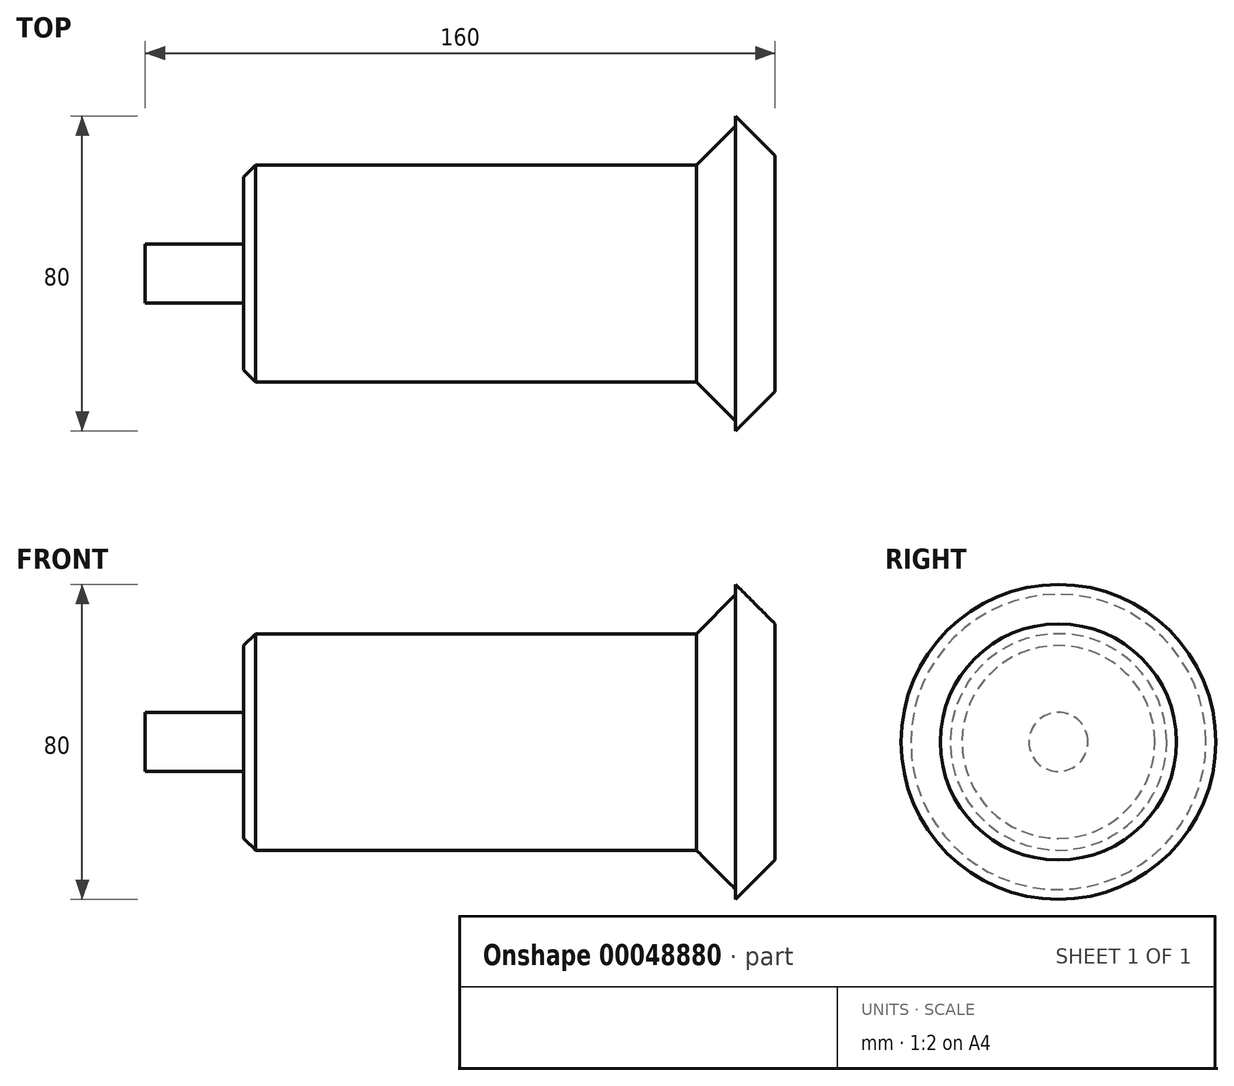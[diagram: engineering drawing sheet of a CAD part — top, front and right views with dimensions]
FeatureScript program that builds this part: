
annotation { "Feature Type Name" : "Feature", "Feature Type Description" : "" }
export const myFeature = defineFeature(function(context is Context, id is Id, definition is map)
    precondition{}
    {
        {
            var Q0;
            Q0=qCreatedBy(makeId("Top.planeOp"),FACE);
            var sketch = newSketch(context, id + "F0", { "sketchPlane" : qUnion([Q0])});
            skLineSegment(sketch, "E0", {"start": v(0, 0) * mm, "end": v(0, 7.5) * mm});
            skLineSegment(sketch, "E1", {"start": v(0, 7.5) * mm, "end": v(25, 7.5) * mm});
            skLineSegment(sketch, "E2", {"start": v(25, 7.5) * mm, "end": v(25, 27.5) * mm});
            skLineSegment(sketch, "E3", {"start": v(25, 27.5) * mm, "end": v(150, 27.5) * mm});
            skLineSegment(sketch, "E4", {"start": v(150, 27.5) * mm, "end": v(150, 40) * mm});
            skLineSegment(sketch, "E5", {"start": v(150, 40) * mm, "end": v(160, 40) * mm});
            skLineSegment(sketch, "E6", {"start": v(160, 40) * mm, "end": v(160, 0) * mm});
            skLineSegment(sketch, "E7", {"start": v(160, 0) * mm, "end": v(0, 0) * mm});
            skSolve(sketch);
        }
        {
            var Q0;
            Q0=makeQuery(id+"F0.imprint","IMPRINT",FACE,{"disambiguationData":[TD([[makeQuery(id+"F0.imprint","IMPRINT",EDGE,{"derivedFrom":sQuery(id+"F0.wireOp",EDGE,"E0")}),-1.0]])]});
            var Q1;
            Q1=sQuery(id+"F0.wireOp",EDGE,"E7");
            revolve(context, id + "F1", {"entities" : qUnion([Q0]), "axis" : qUnion([Q1]), "revolveType" : RevolveType.FULL});
        }
        {
            var Q0;
            Q0=makeQuery(id+"F1.opRevolve","SWEPT_EDGE",EDGE,{"disambiguationData":[OSD([sQuery(id+"F0.wireOp",EDGE,"E5"),sQuery(id+"F0.wireOp",EDGE,"E6")])]});
            var Q1;
            Q1=makeQuery(id+"F1.opRevolve","SWEPT_EDGE",EDGE,{"disambiguationData":[OSD([sQuery(id+"F0.wireOp",EDGE,"E3"),sQuery(id+"F0.wireOp",EDGE,"E4")])]});
            chamfer(context, id + "F2", {"entities" : qUnion([Q0, Q1]), "width" : 10 * mm, "tangentPropagation" : true});
        }
        {
            var Q0;
            Q0=makeQuery(id+"F1.opRevolve","SWEPT_EDGE",EDGE,{"disambiguationData":[OSD([sQuery(id+"F0.wireOp",EDGE,"E2"),sQuery(id+"F0.wireOp",EDGE,"E3")])]});
            chamfer(context, id + "F3", {"entities" : qUnion([Q0]), "width" : 3 * mm, "tangentPropagation" : true});
        }
    });
